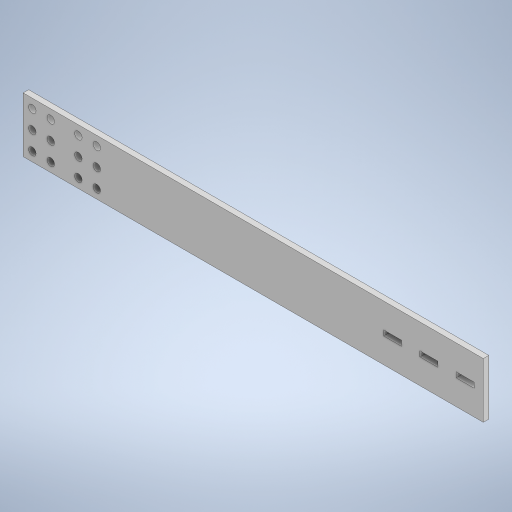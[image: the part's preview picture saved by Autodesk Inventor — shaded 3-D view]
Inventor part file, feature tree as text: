
AUTODESK INVENTOR PART (.ipt)
format: ipt  version: 2023 (Build 270158000, 158)  size: 288,256 bytes
history: native  units: mm
features: extrude x1, sketch x1
ambient origin geometry x8: Origin, YZ Plane, XZ Plane, XY Plane, X Axis, Y Axis, Z Axis, Center Point
bodies: Body1 (feature_tree)
feature tree (2):
  extrude  "Extrusion2"  Depth=6.0mm
  sketch  "Sketch1"  dims[d0=250.0mm d1=30.0mm d2=10.0mm d3=20.0mm d4=20.0mm d5=8.0mm d6=8.0mm d7=8.0mm d8=20.0mm d9=8.0mm d10=8.0mm d11=8.0mm d12=30.0mm d13=20.0mm d14=8.0mm d15=8.0mm d16=8.0mm d17=8.0mm d18=8.0mm d19=8.0mm d20=10.0mm d21=9.7mm d22=2.85mm d25=20.0mm d26=9.7mm d27=20.0mm d28=9.7mm d29=6.0mm d30=0.0mm]
